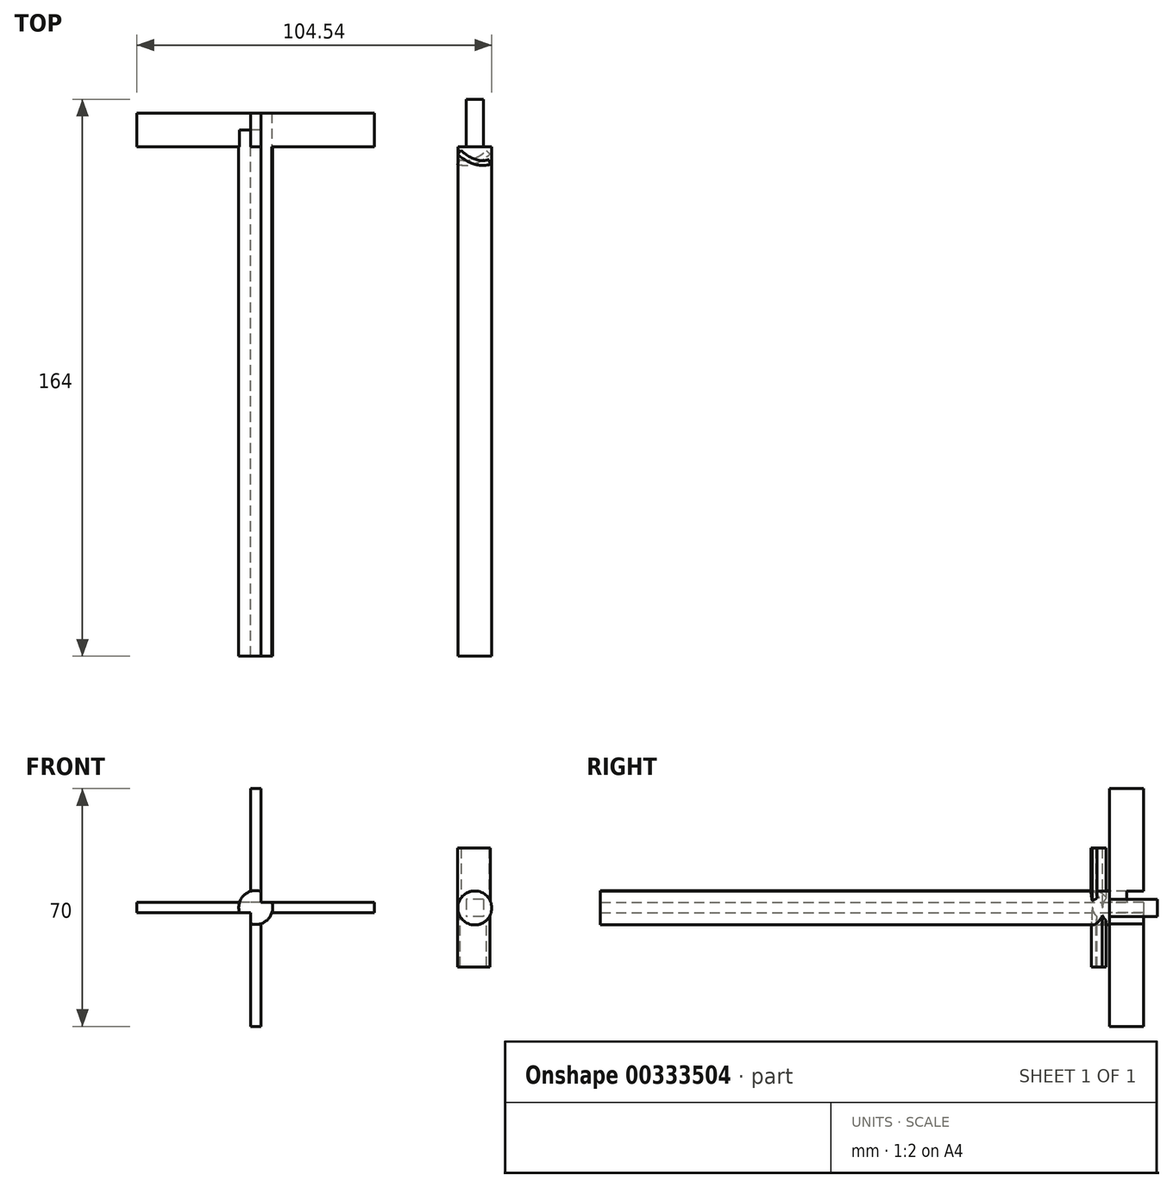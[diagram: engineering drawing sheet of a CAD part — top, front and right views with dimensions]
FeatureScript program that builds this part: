
annotation { "Feature Type Name" : "Feature", "Feature Type Description" : "" }
export const myFeature = defineFeature(function(context is Context, id is Id, definition is map)
    precondition{}
    {
        {
            var Q0;
            Q0=qCreatedBy(makeId("Front.planeOp"),FACE);
            var sketch = newSketch(context, id + "F0", { "sketchPlane" : qUnion([Q0])});
            skCircle(sketch, "E0", {"center": v(0, 0) * mm, "radius": 5 * mm});
            skCircle(sketch, "E1", {"center": v(64.54, -0.12) * mm, "radius": 5 * mm});
            skLineSegment(sketch, "E2.bottom", {"start": v(1.5, 35) * mm, "end": v(-1.5, 35) * mm});
            skLineSegment(sketch, "E2.top", {"start": v(1.5, -35) * mm, "end": v(-1.5, -35) * mm});
            skLineSegment(sketch, "E2.left", {"start": v(1.5, 35) * mm, "end": v(1.5, -35) * mm});
            skLineSegment(sketch, "E2.right", {"start": v(-1.5, 35) * mm, "end": v(-1.5, -35) * mm});
            skLineSegment(sketch, "E3.bottom", {"start": v(35, 1.5) * mm, "end": v(-35, 1.5) * mm});
            skLineSegment(sketch, "E3.top", {"start": v(35, -1.5) * mm, "end": v(-35, -1.5) * mm});
            skLineSegment(sketch, "E3.left", {"start": v(35, 1.5) * mm, "end": v(35, -1.5) * mm});
            skLineSegment(sketch, "E3.right", {"start": v(-35, 1.5) * mm, "end": v(-35, -1.5) * mm});
            skLineSegment(sketch, "E4.bottom", {"start": v(67.04, 2.38) * mm, "end": v(62.04, 2.38) * mm});
            skLineSegment(sketch, "E4.top", {"start": v(67.04, -2.62) * mm, "end": v(62.04, -2.62) * mm});
            skLineSegment(sketch, "E4.left", {"start": v(67.04, 2.38) * mm, "end": v(67.04, -2.62) * mm});
            skLineSegment(sketch, "E4.right", {"start": v(62.04, 2.38) * mm, "end": v(62.04, -2.62) * mm});
            skSolve(sketch);
        }
        {
            var Q0;
            Q0=makeQuery(id+"F0.imprint","IMPRINT",FACE,{"disambiguationData":[TD([[makeQuery(id+"F0.imprint","IMPRINT",EDGE,{"derivedFrom":sQuery(id+"F0.wireOp",EDGE,"JNS3i6Q9-ciBY-eb62-YShs-XhDp9fLNFMLW")}),1.0]])]});
            var Q1;
            Q1=makeQuery(id+"F0.imprint","IMPRINT",FACE,{"disambiguationData":[TD([[makeQuery(id+"F0.imprint","IMPRINT",EDGE,{"derivedFrom":sQuery(id+"F0.wireOp",EDGE,"E1")}),1.0]])]});
            var Q2;
            {var subQ5=sQuery(id+"F0.wireOp",EDGE,"pBVDvmo6-rH54-haC0-Aokm-I5wunjaL656W.bottom");Q2=makeQuery(id+"F0.imprint","IMPRINT",FACE,{"disambiguationData":[TD([[makeQuery(id+"F0.imprint","IMPRINT",EDGE,{"derivedFrom":subQ5}),1.0]])]});}
            var Q3;
            {var subQ0=sQuery(id+"F0.wireOp",EDGE,"Gs2B79kJ-XTI0-SS6X-XdO1-zSeGa6TtnNME.right");Q3=makeQuery(id+"F0.imprint","IMPRINT",FACE,{"disambiguationData":[TD([[makeQuery(id+"F0.imprint","IMPRINT",EDGE,{"derivedFrom":subQ0}),-1.0]])]});}
            var Q4;
            {var subQ0=sQuery(id+"F0.wireOp",EDGE,"Gs2B79kJ-XTI0-SS6X-XdO1-zSeGa6TtnNME.left");Q4=makeQuery(id+"F0.imprint","IMPRINT",FACE,{"disambiguationData":[TD([[makeQuery(id+"F0.imprint","IMPRINT",EDGE,{"derivedFrom":subQ0}),1.0]])]});}
            var Q5;
            {var subQ5=sQuery(id+"F0.wireOp",EDGE,"pBVDvmo6-rH54-haC0-Aokm-I5wunjaL656W.top");Q5=makeQuery(id+"F0.imprint","IMPRINT",FACE,{"disambiguationData":[TD([[makeQuery(id+"F0.imprint","IMPRINT",EDGE,{"derivedFrom":subQ5}),-1.0]])]});}
            var Q6;
            {var subQ0=sQuery(id+"F0.wireOp",EDGE,"pBVDvmo6-rH54-haC0-Aokm-I5wunjaL656W.right");var subQ1=sQuery(id+"F0.wireOp",EDGE,"Gs2B79kJ-XTI0-SS6X-XdO1-zSeGa6TtnNME.bottom");var subQ2=makeQuery(id+"F0.imprint","INTERSECT",VERTEX,{"derivedFrom":[subQ1,subQ0]});Q6=makeQuery(id+"F0.imprint","IMPRINT",FACE,{"disambiguationData":[TD([[makeQuery(id+"F0.imprint","IMPRINT",EDGE,{"disambiguationData":[TD([[subQ2,-1.0]])],"derivedFrom":subQ1}),-1.0]])]});}
            var Q7;
            Q7=makeQuery(id+"F0.imprint","IMPRINT",FACE,{"disambiguationData":[TD([[makeQuery(id+"F0.imprint","IMPRINT",EDGE,{"derivedFrom":sQuery(id+"F0.wireOp",EDGE,"E4.bottom")}),1.0]])]});
            extrude(context, id + "F1", {"entities" : qUnion([Q0, Q1, Q2, Q3, Q4, Q5, Q6, Q7]), "depth" : 150 * mm});
        }
        {
            var Q0;
            {var subQ0=sQuery(id+"F0.wireOp",EDGE,"E3.bottom");var subQ1=sQuery(id+"F0.wireOp",EDGE,"E0");var subQ2=makeQuery(id+"F0.imprint","INTERSECT",VERTEX,{"disambiguationData":[OD(0.0)],"derivedFrom":[subQ1,subQ0]});Q0=makeQuery(id+"F0.imprint","IMPRINT",FACE,{"disambiguationData":[TD([[makeQuery(id+"F0.imprint","IMPRINT",EDGE,{"disambiguationData":[TD([[subQ2,1.0]])],"derivedFrom":subQ1}),1.0]])]});}
            var Q1;
            {var subQ0=sQuery(id+"F0.wireOp",EDGE,"E2.left");var subQ1=sQuery(id+"F0.wireOp",EDGE,"E0");var subQ2=makeQuery(id+"F0.imprint","INTERSECT",VERTEX,{"disambiguationData":[OD(0.0)],"derivedFrom":[subQ1,subQ0]});Q1=makeQuery(id+"F0.imprint","IMPRINT",FACE,{"disambiguationData":[TD([[makeQuery(id+"F0.imprint","IMPRINT",EDGE,{"disambiguationData":[TD([[subQ2,1.0]])],"derivedFrom":subQ1}),1.0]])]});}
            var Q2;
            {var subQ0=sQuery(id+"F0.wireOp",EDGE,"E2.left");var subQ1=sQuery(id+"F0.wireOp",EDGE,"E0");var subQ2=makeQuery(id+"F0.imprint","INTERSECT",VERTEX,{"disambiguationData":[OD(0.0)],"derivedFrom":[subQ1,subQ0]});Q2=makeQuery(id+"F0.imprint","IMPRINT",FACE,{"disambiguationData":[TD([[makeQuery(id+"F0.imprint","IMPRINT",EDGE,{"disambiguationData":[TD([[subQ2,-1.0]])],"derivedFrom":subQ1}),1.0]])]});}
            var Q3;
            {var subQ0=sQuery(id+"F0.wireOp",EDGE,"E2.right");var subQ1=sQuery(id+"F0.wireOp",EDGE,"E0");var subQ2=makeQuery(id+"F0.imprint","INTERSECT",VERTEX,{"disambiguationData":[OD(0.0)],"derivedFrom":[subQ1,subQ0]});Q3=makeQuery(id+"F0.imprint","IMPRINT",FACE,{"disambiguationData":[TD([[makeQuery(id+"F0.imprint","IMPRINT",EDGE,{"disambiguationData":[TD([[subQ2,-1.0]])],"derivedFrom":subQ1}),1.0]])]});}
            var Q4;
            {var subQ0=sQuery(id+"F0.wireOp",EDGE,"E3.bottom");var subQ1=sQuery(id+"F0.wireOp",EDGE,"E0");var subQ2=makeQuery(id+"F0.imprint","INTERSECT",VERTEX,{"disambiguationData":[OD(1.0)],"derivedFrom":[subQ1,subQ0]});Q4=makeQuery(id+"F0.imprint","IMPRINT",FACE,{"disambiguationData":[TD([[makeQuery(id+"F0.imprint","IMPRINT",EDGE,{"disambiguationData":[TD([[subQ2,-1.0]])],"derivedFrom":subQ1}),1.0]])]});}
            var Q5;
            {var subQ0=sQuery(id+"F0.wireOp",EDGE,"E3.bottom");var subQ1=sQuery(id+"F0.wireOp",EDGE,"E2.left");var subQ2=makeQuery(id+"F0.imprint","INTERSECT",VERTEX,{"derivedFrom":[subQ1,subQ0]});Q5=makeQuery(id+"F0.imprint","IMPRINT",FACE,{"disambiguationData":[TD([[makeQuery(id+"F0.imprint","IMPRINT",EDGE,{"disambiguationData":[TD([[subQ2,-1.0]])],"derivedFrom":subQ1}),-1.0]])]});}
            var Q6;
            {var subQ0=sQuery(id+"F0.wireOp",EDGE,"E2.left");var subQ1=sQuery(id+"F0.wireOp",EDGE,"E0");var subQ2=makeQuery(id+"F0.imprint","INTERSECT",VERTEX,{"disambiguationData":[OD(1.0)],"derivedFrom":[subQ1,subQ0]});Q6=makeQuery(id+"F0.imprint","IMPRINT",FACE,{"disambiguationData":[TD([[makeQuery(id+"F0.imprint","IMPRINT",EDGE,{"disambiguationData":[TD([[subQ2,-1.0]])],"derivedFrom":subQ1}),1.0]])]});}
            var Q7;
            {var subQ0=sQuery(id+"F0.wireOp",EDGE,"E2.right");var subQ1=sQuery(id+"F0.wireOp",EDGE,"E0");var subQ2=makeQuery(id+"F0.imprint","INTERSECT",VERTEX,{"disambiguationData":[OD(1.0)],"derivedFrom":[subQ1,subQ0]});Q7=makeQuery(id+"F0.imprint","IMPRINT",FACE,{"disambiguationData":[TD([[makeQuery(id+"F0.imprint","IMPRINT",EDGE,{"disambiguationData":[TD([[subQ2,-1.0]])],"derivedFrom":subQ1}),1.0]])]});}
            var Q8;
            {var subQ0=sQuery(id+"F0.wireOp",EDGE,"E3.top");var subQ1=sQuery(id+"F0.wireOp",EDGE,"E0");var subQ2=makeQuery(id+"F0.imprint","INTERSECT",VERTEX,{"disambiguationData":[OD(0.0)],"derivedFrom":[subQ1,subQ0]});Q8=makeQuery(id+"F0.imprint","IMPRINT",FACE,{"disambiguationData":[TD([[makeQuery(id+"F0.imprint","IMPRINT",EDGE,{"disambiguationData":[TD([[subQ2,-1.0]])],"derivedFrom":subQ1}),1.0]])]});}
            extrude(context, id + "F2", {"entities" : qUnion([Q0, Q1, Q2, Q3, Q4, Q5, Q6, Q7, Q8]), "depth" : 150 * mm});
        }
        {
            var Q0;
            {var subQ5=sQuery(id+"F0.wireOp",EDGE,"E3.right");Q0=makeQuery(id+"F0.imprint","IMPRINT",FACE,{"disambiguationData":[TD([[makeQuery(id+"F0.imprint","IMPRINT",EDGE,{"derivedFrom":subQ5}),1.0]])]});}
            var Q1;
            {var subQ5=sQuery(id+"F0.wireOp",EDGE,"E2.bottom");Q1=makeQuery(id+"F0.imprint","IMPRINT",FACE,{"disambiguationData":[TD([[makeQuery(id+"F0.imprint","IMPRINT",EDGE,{"derivedFrom":subQ5}),1.0]])]});}
            var Q2;
            {var subQ0=sQuery(id+"F0.wireOp",EDGE,"E3.bottom");var subQ1=sQuery(id+"F0.wireOp",EDGE,"E0");var subQ2=makeQuery(id+"F0.imprint","INTERSECT",VERTEX,{"disambiguationData":[OD(1.0)],"derivedFrom":[subQ1,subQ0]});Q2=makeQuery(id+"F0.imprint","IMPRINT",FACE,{"disambiguationData":[TD([[makeQuery(id+"F0.imprint","IMPRINT",EDGE,{"disambiguationData":[TD([[subQ2,-1.0]])],"derivedFrom":subQ1}),1.0]])]});}
            var Q3;
            {var subQ0=sQuery(id+"F0.wireOp",EDGE,"E2.left");var subQ1=sQuery(id+"F0.wireOp",EDGE,"E0");var subQ2=makeQuery(id+"F0.imprint","INTERSECT",VERTEX,{"disambiguationData":[OD(0.0)],"derivedFrom":[subQ1,subQ0]});Q3=makeQuery(id+"F0.imprint","IMPRINT",FACE,{"disambiguationData":[TD([[makeQuery(id+"F0.imprint","IMPRINT",EDGE,{"disambiguationData":[TD([[subQ2,-1.0]])],"derivedFrom":subQ1}),1.0]])]});}
            var Q4;
            {var subQ0=sQuery(id+"F0.wireOp",EDGE,"E3.bottom");var subQ1=sQuery(id+"F0.wireOp",EDGE,"E2.left");var subQ2=makeQuery(id+"F0.imprint","INTERSECT",VERTEX,{"derivedFrom":[subQ1,subQ0]});Q4=makeQuery(id+"F0.imprint","IMPRINT",FACE,{"disambiguationData":[TD([[makeQuery(id+"F0.imprint","IMPRINT",EDGE,{"disambiguationData":[TD([[subQ2,-1.0]])],"derivedFrom":subQ1}),-1.0]])]});}
            var Q5;
            {var subQ5=sQuery(id+"F0.wireOp",EDGE,"E2.top");Q5=makeQuery(id+"F0.imprint","IMPRINT",FACE,{"disambiguationData":[TD([[makeQuery(id+"F0.imprint","IMPRINT",EDGE,{"derivedFrom":subQ5}),-1.0]])]});}
            var Q6;
            {var subQ0=sQuery(id+"F0.wireOp",EDGE,"E2.right");var subQ1=sQuery(id+"F0.wireOp",EDGE,"E0");var subQ2=makeQuery(id+"F0.imprint","INTERSECT",VERTEX,{"disambiguationData":[OD(1.0)],"derivedFrom":[subQ1,subQ0]});Q6=makeQuery(id+"F0.imprint","IMPRINT",FACE,{"disambiguationData":[TD([[makeQuery(id+"F0.imprint","IMPRINT",EDGE,{"disambiguationData":[TD([[subQ2,-1.0]])],"derivedFrom":subQ1}),1.0]])]});}
            var Q7;
            {var subQ0=sQuery(id+"F0.wireOp",EDGE,"E3.bottom");var subQ1=sQuery(id+"F0.wireOp",EDGE,"E0");var subQ2=makeQuery(id+"F0.imprint","INTERSECT",VERTEX,{"disambiguationData":[OD(0.0)],"derivedFrom":[subQ1,subQ0]});Q7=makeQuery(id+"F0.imprint","IMPRINT",FACE,{"disambiguationData":[TD([[makeQuery(id+"F0.imprint","IMPRINT",EDGE,{"disambiguationData":[TD([[subQ2,1.0]])],"derivedFrom":subQ1}),1.0]])]});}
            var Q8;
            {var subQ5=sQuery(id+"F0.wireOp",EDGE,"E3.left");Q8=makeQuery(id+"F0.imprint","IMPRINT",FACE,{"disambiguationData":[TD([[makeQuery(id+"F0.imprint","IMPRINT",EDGE,{"derivedFrom":subQ5}),-1.0]])]});}
            extrude(context, id + "F3", {"entities" : qUnion([Q0, Q1, Q2, Q3, Q4, Q5, Q6, Q7, Q8]), "operationType" : NewBodyOperationType.ADD, "oppositeDirection" : true, "depth" : 10 * mm});
        }
        {
            var Q0;
            {var subQ0=sQuery(id+"F0.wireOp",EDGE,"E3.top");var subQ1=sQuery(id+"F0.wireOp",EDGE,"E0");var subQ2=makeQuery(id+"F0.imprint","INTERSECT",VERTEX,{"disambiguationData":[OD(0.0)],"derivedFrom":[subQ1,subQ0]});Q0=makeQuery(id+"F0.imprint","IMPRINT",FACE,{"disambiguationData":[TD([[makeQuery(id+"F0.imprint","IMPRINT",EDGE,{"disambiguationData":[TD([[subQ2,-1.0]])],"derivedFrom":subQ1}),1.0]])]});}
            var Q1;
            {var subQ0=sQuery(id+"F0.wireOp",EDGE,"E2.left");var subQ1=sQuery(id+"F0.wireOp",EDGE,"E0");var subQ2=makeQuery(id+"F0.imprint","INTERSECT",VERTEX,{"disambiguationData":[OD(1.0)],"derivedFrom":[subQ1,subQ0]});Q1=makeQuery(id+"F0.imprint","IMPRINT",FACE,{"disambiguationData":[TD([[makeQuery(id+"F0.imprint","IMPRINT",EDGE,{"disambiguationData":[TD([[subQ2,-1.0]])],"derivedFrom":subQ1}),1.0]])]});}
            var Q2;
            {var subQ0=sQuery(id+"F0.wireOp",EDGE,"E2.left");var subQ1=sQuery(id+"F0.wireOp",EDGE,"E0");var subQ2=makeQuery(id+"F0.imprint","INTERSECT",VERTEX,{"disambiguationData":[OD(0.0)],"derivedFrom":[subQ1,subQ0]});Q2=makeQuery(id+"F0.imprint","IMPRINT",FACE,{"disambiguationData":[TD([[makeQuery(id+"F0.imprint","IMPRINT",EDGE,{"disambiguationData":[TD([[subQ2,1.0]])],"derivedFrom":subQ1}),1.0]])]});}
            var Q3;
            {var subQ0=sQuery(id+"F0.wireOp",EDGE,"E2.right");var subQ1=sQuery(id+"F0.wireOp",EDGE,"E0");var subQ2=makeQuery(id+"F0.imprint","INTERSECT",VERTEX,{"disambiguationData":[OD(0.0)],"derivedFrom":[subQ1,subQ0]});Q3=makeQuery(id+"F0.imprint","IMPRINT",FACE,{"disambiguationData":[TD([[makeQuery(id+"F0.imprint","IMPRINT",EDGE,{"disambiguationData":[TD([[subQ2,-1.0]])],"derivedFrom":subQ1}),1.0]])]});}
            extrude(context, id + "F4", {"entities" : qUnion([Q0, Q1, Q2, Q3]), "operationType" : NewBodyOperationType.ADD, "oppositeDirection" : true, "depth" : 5 * mm});
        }
        {
            var Q0;
            Q0=makeQuery(id+"F0.imprint","IMPRINT",FACE,{"disambiguationData":[TD([[makeQuery(id+"F0.imprint","IMPRINT",EDGE,{"derivedFrom":sQuery(id+"F0.wireOp",EDGE,"E4.bottom")}),1.0]])]});
            extrude(context, id + "F5", {"entities" : qUnion([Q0]), "operationType" : NewBodyOperationType.ADD, "oppositeDirection" : true, "depth" : 14 * mm});
        }
        {
            var Q0;
            Q0=makeQuery(id+"F2.opExtrude","CAP_FACE",FACE,{"disambiguationData":[OSD([sQuery(id+"F0.wireOp",EDGE,"E0")])],"isStart":false});
            var sketch = newSketch(context, id + "F6", { "sketchPlane" : qUnion([Q0])});
            skSolve(sketch);
        }
        {
            var Q0;
            Q0=qCreatedBy(makeId("Top.planeOp"),FACE);
            var sketch = newSketch(context, id + "F7", { "sketchPlane" : qUnion([Q0])});
            skPoint(sketch, "E5.1.internal.snap0", {"position": v(64.24, -3.5) * mm});
            skFitSpline(sketch, "E5", {"points": [v(59.44, -5.12) * mm, v(64.24, -5) * mm, v(69.04, -2.14) * mm], "startDerivative": vector(10.28, -2.84) * mm, "endDerivative": vector(9.1, 7.71) * mm});
            skFitSpline(sketch, "E6.0", {"points": [v(59.83, -3.67) * mm, v(60.54, -3.87) * mm, v(61.92, -4.02) * mm, v(63.6, -3.7) * mm, v(64.95, -3.14) * mm, v(66.3, -2.39) * mm, v(67.35, -1.6) * mm, v(68.07, -1) * mm]});
            skLineSegment(sketch, "E7", {"start": v(67.96, -1.09) * mm, "end": v(69.04, -2.14) * mm});
            skLineSegment(sketch, "E8", {"start": v(60.22, -3.77) * mm, "end": v(59.44, -5.12) * mm});
            skSolve(sketch);
        }
        {
            var Q0;
            Q0=qCreatedBy(makeId("Top.planeOp"),FACE);
            var sketch = newSketch(context, id + "F8", { "sketchPlane" : qUnion([Q0])});
            skFitSpline(sketch, "E9.MirrorCS", {"points": [v(69.08, -5.16) * mm, v(64.27, -5.06) * mm, v(59.48, -2.19) * mm], "startDerivative": vector(-10.28, -2.84) * mm, "endDerivative": vector(-9.1, 7.71) * mm});
            skFitSpline(sketch, "E10.0", {"points": [v(68.68, -3.72) * mm, v(67.97, -3.91) * mm, v(66.59, -4.06) * mm, v(64.9, -3.74) * mm, v(63.57, -3.19) * mm, v(62.2, -2.43) * mm, v(61.16, -1.65) * mm, v(60.45, -1.05) * mm]});
            skLineSegment(sketch, "E11", {"start": v(68.68, -3.72) * mm, "end": v(69.08, -5.16) * mm});
            skLineSegment(sketch, "E12", {"start": v(60.45, -1.05) * mm, "end": v(59.48, -2.19) * mm});
            skSolve(sketch);
        }
        {
            var Q0;
            Q0=qSketchRegion(id+"F7",true);
            extrude(context, id + "F9", {"entities" : qUnion([Q0]), "operationType" : NewBodyOperationType.ADD, "oppositeDirection" : true, "depth" : 17.5 * mm});
        }
        {
            var Q0;
            Q0=qSketchRegion(id+"F8",true);
            extrude(context, id + "F10", {"entities" : qUnion([Q0]), "operationType" : NewBodyOperationType.ADD, "depth" : 17.5 * mm});
        }
        {
            var Q0;
            Q0=makeQuery(id+"F6.imprint","IMPRINT",FACE,{"disambiguationData":[TD([[makeQuery(id+"F6.imprint","IMPRINT",EDGE,{"derivedFrom":makeQuery(id+"F2.opExtrude","CAP_EDGE",EDGE,{"disambiguationData":[OSD([sQuery(id+"F0.wireOp",EDGE,"E0")])],"isStart":false})}),1.0]])]});
            var sketch = newSketch(context, id + "F11", { "sketchPlane" : qUnion([Q0])});
            skLineSegment(sketch, "E13.bottom", {"start": v(-2.6, 2.6) * mm, "end": v(2.6, 2.6) * mm});
            skLineSegment(sketch, "E13.top", {"start": v(-2.6, -2.6) * mm, "end": v(2.6, -2.6) * mm});
            skLineSegment(sketch, "E13.left", {"start": v(-2.6, 2.6) * mm, "end": v(-2.6, -2.6) * mm});
            skLineSegment(sketch, "E13.right", {"start": v(2.6, 2.6) * mm, "end": v(2.6, -2.6) * mm});
            skPoint(sketch, "E13.middle", {"position": v(0, 0) * mm});
            skSolve(sketch);
        }
        {
            var Q0;
            Q0=makeQuery(id+"F11.imprint","IMPRINT",FACE,{"disambiguationData":[TD([[makeQuery(id+"F11.imprint","IMPRINT",EDGE,{"derivedFrom":sQuery(id+"F11.wireOp",EDGE,"E13.bottom")}),-1.0]])]});
            extrude(context, id + "F12", {"entities" : qUnion([Q0]), "operationType" : NewBodyOperationType.REMOVE, "oppositeDirection" : true, "depth" : 15 * mm});
        }
    });
